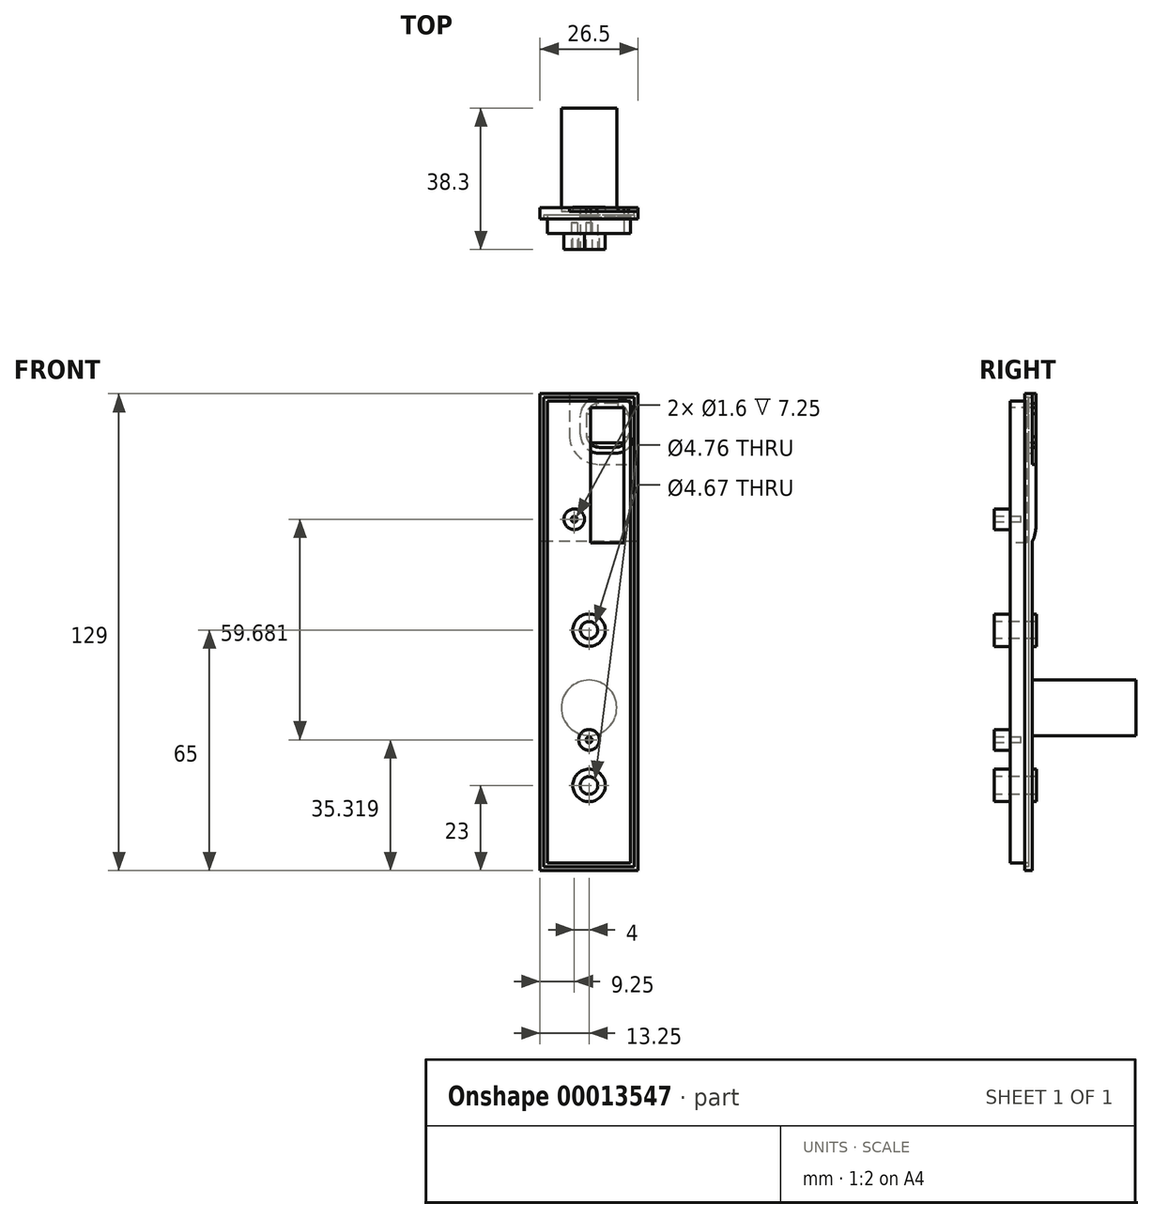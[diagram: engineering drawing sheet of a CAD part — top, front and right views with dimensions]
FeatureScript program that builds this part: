
annotation { "Feature Type Name" : "Feature", "Feature Type Description" : "" }
export const myFeature = defineFeature(function(context is Context, id is Id, definition is map)
    precondition{}
    {
        {
            var Q0;
            Q0=qCreatedBy(makeId("Front.planeOp"),FACE);
            var sketch = newSketch(context, id + "F0", { "sketchPlane" : qUnion([Q0])});
            skLineSegment(sketch, "E0.rect.bottom", {"start": v(13.25, -64.5) * mm, "end": v(-13.25, -64.5) * mm});
            skLineSegment(sketch, "E0.rect.top", {"start": v(13.25, 64.5) * mm, "end": v(-13.25, 64.5) * mm});
            skLineSegment(sketch, "E0.rect.left", {"start": v(13.25, -64.5) * mm, "end": v(13.25, 64.5) * mm});
            skLineSegment(sketch, "E0.rect.right", {"start": v(-13.25, -64.5) * mm, "end": v(-13.25, 64.5) * mm});
            skPoint(sketch, "E0.rect.middle", {"position": v(0, 0) * mm});
            skSolve(sketch);
        }
        {
            var Q0;
            Q0 = qSketchRegion(id + "F0", true);
            extrude(context, id + "F1", {"entities" : qUnion([Q0]), "depth" : 2 * mm});
        }
        {
            var Q0;
            Q0=makeQuery(id+"F1.opExtrude","CAP_FACE",FACE,{"disambiguationData":[OSD([sQuery(id+"F0.wireOp",EDGE,"E0.rect.bottom"),sQuery(id+"F0.wireOp",EDGE,"E0.rect.top"),sQuery(id+"F0.wireOp",EDGE,"E0.rect.left"),sQuery(id+"F0.wireOp",EDGE,"E0.rect.right")])],"isStart":false});
            var sketch = newSketch(context, id + "F2", { "sketchPlane" : qUnion([Q0])});
            skLineSegment(sketch, "E1.rect.bottom", {"start": v(12.25, 63.5) * mm, "end": v(-12.25, 63.5) * mm});
            skLineSegment(sketch, "E1.rect.top", {"start": v(12.25, -63.5) * mm, "end": v(-12.25, -63.5) * mm});
            skLineSegment(sketch, "E1.rect.left", {"start": v(12.25, 63.5) * mm, "end": v(12.25, -63.5) * mm});
            skLineSegment(sketch, "E1.rect.right", {"start": v(-12.25, 63.5) * mm, "end": v(-12.25, -63.5) * mm});
            skPoint(sketch, "E1.rect.middle", {"position": v(0, 0) * mm});
            skLineSegment(sketch, "E2.rect.bottom", {"start": v(11.25, 62.5) * mm, "end": v(-11.25, 62.5) * mm});
            skLineSegment(sketch, "E2.rect.top", {"start": v(11.25, -62.5) * mm, "end": v(-11.25, -62.5) * mm});
            skLineSegment(sketch, "E2.rect.left", {"start": v(11.25, 62.5) * mm, "end": v(11.25, -62.5) * mm});
            skLineSegment(sketch, "E2.rect.right", {"start": v(-11.25, 62.5) * mm, "end": v(-11.25, -62.5) * mm});
            skSolve(sketch);
        }
        {
            var Q0;
            Q0 = qSketchRegion(id + "F2", true);
            extrude(context, id + "F3", {"entities" : qUnion([Q0]), "operationType" : NewBodyOperationType.REMOVE, "oppositeDirection" : true, "depth" : 1 * mm});
        }
        {
            var Q0;
            Q0=makeQuery(id+"F1.opExtrude","CAP_FACE",FACE,{"disambiguationData":[OSD([sQuery(id+"F0.wireOp",EDGE,"E0.rect.bottom"),sQuery(id+"F0.wireOp",EDGE,"E0.rect.top"),sQuery(id+"F0.wireOp",EDGE,"E0.rect.left"),sQuery(id+"F0.wireOp",EDGE,"E0.rect.right")])],"isStart":true});
            var sketch = newSketch(context, id + "F4", { "sketchPlane" : qUnion([Q0])});
            skLineSegment(sketch, "E3.bottom", {"start": v(-13.25, 64.5) * mm, "end": v(13.25, 64.5) * mm});
            skLineSegment(sketch, "E3.top", {"start": v(-13.25, 24.5) * mm, "end": v(13.25, 24.5) * mm});
            skLineSegment(sketch, "E3.left", {"start": v(-13.25, 64.5) * mm, "end": v(-13.25, 24.5) * mm});
            skLineSegment(sketch, "E3.right", {"start": v(13.25, 64.5) * mm, "end": v(13.25, 24.5) * mm});
            skSolve(sketch);
        }
        {
            var Q0;
            Q0 = qSketchRegion(id + "F4", true);
            extrude(context, id + "F5", {"entities" : qUnion([Q0]), "operationType" : NewBodyOperationType.ADD, "depth" : 1 * mm});
        }
        {
            var Q0;
            Q0=makeQuery(id+"F5.opExtrude","CAP_EDGE",EDGE,{"disambiguationData":[OSD([sQuery(id+"F4.wireOp",EDGE,"E3.top")])],"isStart":false});
            fillet(context, id + "F6", {"entities" : qUnion([Q0]), "radius" : 10 * mm, "tangentPropagation" : true, "allowEdgeOverflow" : false});
        }
        {
            var Q0;
            Q0=makeQuery(id+"F3.boolean.opBoolean","SPLIT",FACE,{"disambiguationData":[TD([makeQuery(id+"F3.opExtrude","SWEPT_FACE",FACE,{"disambiguationData":[OSD([sQuery(id+"F2.wireOp",EDGE,"E2.rect.bottom")])]})])],"derivedFrom":makeQuery(id+"F1.opExtrude","CAP_FACE",FACE,{"disambiguationData":[OSD([sQuery(id+"F0.wireOp",EDGE,"E0.rect.bottom"),sQuery(id+"F0.wireOp",EDGE,"E0.rect.top"),sQuery(id+"F0.wireOp",EDGE,"E0.rect.left"),sQuery(id+"F0.wireOp",EDGE,"E0.rect.right")])],"isStart":false})});
            var sketch = newSketch(context, id + "F7", { "sketchPlane" : qUnion([Q0])});
            skLineSegment(sketch, "E4.bottom", {"start": v(9.45, 60.7) * mm, "end": v(0.45, 60.7) * mm});
            skLineSegment(sketch, "E4.top", {"start": v(0.45, 51.18) * mm, "end": v(9.45, 51.18) * mm});
            skLineSegment(sketch, "E4.left", {"start": v(9.45, 60.7) * mm, "end": v(9.45, 51.18) * mm});
            skLineSegment(sketch, "E4.right", {"start": v(0.45, 60.7) * mm, "end": v(0.45, 51.18) * mm});
            skSolve(sketch);
        }
        {
            var Q0;
            Q0=makeQuery(id+"F3.boolean.opBoolean","SPLIT",FACE,{"disambiguationData":[TD([makeQuery(id+"F3.opExtrude","SWEPT_FACE",FACE,{"disambiguationData":[OSD([sQuery(id+"F2.wireOp",EDGE,"E2.rect.bottom")])]})])],"derivedFrom":makeQuery(id+"F1.opExtrude","CAP_FACE",FACE,{"disambiguationData":[OSD([sQuery(id+"F0.wireOp",EDGE,"E0.rect.bottom"),sQuery(id+"F0.wireOp",EDGE,"E0.rect.top"),sQuery(id+"F0.wireOp",EDGE,"E0.rect.left"),sQuery(id+"F0.wireOp",EDGE,"E0.rect.right")])],"isStart":false})});
            var sketch = newSketch(context, id + "F8", { "sketchPlane" : qUnion([Q0])});
            skLineSegment(sketch, "E5.bottom", {"start": v(-11.25, 62.5) * mm, "end": v(11.25, 62.5) * mm});
            skLineSegment(sketch, "E5.top", {"start": v(-11.25, -62.5) * mm, "end": v(11.25, -62.5) * mm});
            skLineSegment(sketch, "E5.left", {"start": v(-11.25, 62.5) * mm, "end": v(-11.25, -62.5) * mm});
            skLineSegment(sketch, "E5.right", {"start": v(11.25, 62.5) * mm, "end": v(11.25, -62.5) * mm});
            skSolve(sketch);
        }
        {
            var Q0;
            Q0 = qSketchRegion(id + "F8", true);
            extrude(context, id + "F9", {"entities" : qUnion([Q0]), "operationType" : NewBodyOperationType.ADD, "depth" : 4 * mm});
        }
        {
            var Q0;
            Q0 = qSketchRegion(id + "F7", true);
            var Q1;
            Q1=makeQuery(id+"F5.opExtrude","CAP_FACE",FACE,{"disambiguationData":[OSD([sQuery(id+"F4.wireOp",EDGE,"E3.bottom"),sQuery(id+"F4.wireOp",EDGE,"E3.top"),sQuery(id+"F4.wireOp",EDGE,"E3.left"),sQuery(id+"F4.wireOp",EDGE,"E3.right")])],"isStart":false});
            extrude(context, id + "F10", {"entities" : qUnion([Q0]), "operationType" : NewBodyOperationType.REMOVE, "endBound" : BoundingType.UP_TO_SURFACE, "oppositeDirection" : true, "endBoundEntityFace" : qUnion([Q1]), "depth" : 25 * mm, "hasSecondDirection" : true, "secondDirectionOppositeDirection" : false, "secondDirectionDepth" : 10 * mm});
        }
        {
            var Q0;
            Q0=makeQuery(id+"F9.opExtrude","CAP_FACE",FACE,{"disambiguationData":[OSD([sQuery(id+"F8.wireOp",EDGE,"E5.bottom"),sQuery(id+"F8.wireOp",EDGE,"E5.top"),sQuery(id+"F8.wireOp",EDGE,"E5.left"),sQuery(id+"F8.wireOp",EDGE,"E5.right")])],"isStart":false});
            var sketch = newSketch(context, id + "F11", { "sketchPlane" : qUnion([Q0])});
            skLineSegment(sketch, "E6.bottom", {"start": v(0.45, 51.18) * mm, "end": v(9.45, 51.18) * mm});
            skLineSegment(sketch, "E6.top", {"start": v(0.45, 24.18) * mm, "end": v(9.45, 24.18) * mm});
            skLineSegment(sketch, "E6.left", {"start": v(0.45, 51.18) * mm, "end": v(0.45, 24.18) * mm});
            skLineSegment(sketch, "E6.right", {"start": v(9.45, 51.18) * mm, "end": v(9.45, 24.18) * mm});
            skSolve(sketch);
        }
        {
            var Q0;
            Q0 = qSketchRegion(id + "F11", true);
            var Q1;
            {var subQ0=sQuery(id+"F2.wireOp",EDGE,"E1.rect.bottom");var subQ1=sQuery(id+"F2.wireOp",EDGE,"E1.rect.top");var subQ2=sQuery(id+"F2.wireOp",EDGE,"E1.rect.left");var subQ3=sQuery(id+"F2.wireOp",EDGE,"E1.rect.right");var subQ4=sQuery(id+"F2.wireOp",EDGE,"E2.rect.bottom");var subQ5=sQuery(id+"F2.wireOp",EDGE,"E2.rect.top");var subQ6=sQuery(id+"F2.wireOp",EDGE,"E2.rect.left");var subQ7=sQuery(id+"F2.wireOp",EDGE,"E2.rect.right");Q1=makeQuery(id+"F26.boolean.opBoolean","SPLIT",FACE,{"disambiguationData":[TD([makeQuery(id+"F3.boolean.opBoolean","COPY",FACE,{"derivedFrom":makeQuery(id+"F3.opExtrude","SWEPT_FACE",FACE,{"disambiguationData":[OSD([subQ1])]})})])],"derivedFrom":makeQuery(id+"F3.boolean.opBoolean","COPY",FACE,{"derivedFrom":makeQuery(id+"F3.opExtrude","CAP_FACE",FACE,{"disambiguationData":[OSD([subQ0,subQ1,subQ2,subQ3,subQ4,subQ5,subQ6,subQ7])],"isStart":false})})});}
            extrude(context, id + "F12", {"entities" : qUnion([Q0]), "operationType" : NewBodyOperationType.REMOVE, "oppositeDirection" : true, "endBoundEntityFace" : qUnion([Q1]), "depth" : 4.5 * mm});
        }
        {
            var Q0;
            Q0=makeQuery(id+"F9.opExtrude","CAP_FACE",FACE,{"disambiguationData":[OSD([sQuery(id+"F8.wireOp",EDGE,"E5.bottom"),sQuery(id+"F8.wireOp",EDGE,"E5.top"),sQuery(id+"F8.wireOp",EDGE,"E5.left"),sQuery(id+"F8.wireOp",EDGE,"E5.right")])],"isStart":false});
            var sketch = newSketch(context, id + "F13", { "sketchPlane" : qUnion([Q0])});
            skLineSegment(sketch, "E7", {"start": v(-13.25, 64.5) * mm, "end": v(13.25, 64.5) * mm, "construction": true});
            skCircle(sketch, "E8", {"center": v(0, 0.5) * mm, "radius": 4.38 * mm});
            skLineSegment(sketch, "E9", {"start": v(-13.25, -84.5) * mm, "end": v(13.25, -84.5) * mm, "construction": true});
            skCircle(sketch, "E10", {"center": v(0, -41.5) * mm, "radius": 4.38 * mm});
            skPoint(sketch, "E11.rect.middle", {"position": v(0, -20.5) * mm});
            skCircle(sketch, "E12", {"center": v(0, -20.5) * mm, "radius": 7.5 * mm, "construction": true});
            skLineSegment(sketch, "E13", {"start": v(0, 64.5) * mm, "end": v(0, -84.5) * mm});
            skLineSegment(sketch, "E14", {"start": v(0, 0.5) * mm, "end": v(0, -20.5) * mm, "construction": true});
            skLineSegment(sketch, "E15", {"start": v(0, -20.5) * mm, "end": v(0, -41.5) * mm, "construction": true});
            skSolve(sketch);
        }
        {
            var Q0;
            Q0 = qSketchRegion(id + "F13", true);
            var Q1;
            Q1=makeQuery(id+"F22.opExtrude","CAP_FACE",FACE,{"disambiguationData":[OSD([sQuery(id+"F21.wireOp",EDGE,"E30")])],"isStart":false});
            extrude(context, id + "F14", {"entities" : qUnion([Q0]), "operationType" : NewBodyOperationType.ADD, "endBoundEntityFace" : qUnion([Q1]), "depth" : 4.3 * mm});
        }
        {
            var Q0;
            {var subQ0=sQuery(id+"F0.wireOp",EDGE,"E0.rect.bottom");var subQ1=sQuery(id+"F0.wireOp",EDGE,"E0.rect.top");var subQ2=sQuery(id+"F0.wireOp",EDGE,"E0.rect.left");var subQ3=sQuery(id+"F0.wireOp",EDGE,"E0.rect.right");Q0=makeQuery(id+"FUutNJTZsO6T2Ni_1.boolean.opBoolean","SPLIT",FACE,{"disambiguationData":[TD([makeQuery(id+"F1.opExtrude","SWEPT_FACE",FACE,{"disambiguationData":[OSD([subQ0])]})])],"derivedFrom":makeQuery(id+"F1.opExtrude","CAP_FACE",FACE,{"disambiguationData":[OSD([subQ0,subQ1,subQ2,subQ3])],"isStart":true})});}
            var sketch = newSketch(context, id + "F15", { "sketchPlane" : qUnion([Q0])});
            skLineSegment(sketch, "E16.rect.bottom", {"start": v(13.25, -64.5) * mm, "end": v(-13.25, -64.5) * mm, "construction": true});
            skPoint(sketch, "E16.rect.middle", {"position": v(0, -20.5) * mm});
            skCircle(sketch, "E17", {"center": v(0, -20.5) * mm, "radius": 7.5 * mm});
            skLineSegment(sketch, "E18.rect.top", {"start": v(13.25, 15) * mm, "end": v(-13.25, 15) * mm, "construction": true});
            skLineSegment(sketch, "E18.rect.left", {"start": v(13.25, -64.5) * mm, "end": v(13.25, 15) * mm, "construction": true});
            skLineSegment(sketch, "E18.rect.right", {"start": v(-13.25, -64.5) * mm, "end": v(-13.25, 15) * mm, "construction": true});
            skLineSegment(sketch, "E19", {"start": v(-13.25, -44.5) * mm, "end": v(13.25, -44.5) * mm, "construction": true});
            skLineSegment(sketch, "E20", {"start": v(0, 15) * mm, "end": v(0, -44.5) * mm});
            skSolve(sketch);
        }
        {
            var Q0;
            Q0 = qSketchRegion(id + "F15", true);
            extrude(context, id + "F16", {"entities" : qUnion([Q0]), "operationType" : NewBodyOperationType.ADD, "depth" : 28 * mm});
        }
        {
            var Q0;
            Q0=makeQuery(id+"F14.opExtrude","CAP_FACE",FACE,{"disambiguationData":[OSD([sQuery(id+"F13.wireOp",EDGE,"E8")])],"isStart":false});
            var sketch = newSketch(context, id + "F17", { "sketchPlane" : qUnion([Q0])});
            skCircle(sketch, "E21", {"center": v(0, 0.5) * mm, "radius": 2.34 * mm});
            skCircle(sketch, "E22", {"center": v(0, -41.5) * mm, "radius": 2.38 * mm});
            skLineSegment(sketch, "E23", {"start": v(-4.38, -23.42) * mm, "end": v(-4.38, -59.58) * mm, "construction": true});
            skLineSegment(sketch, "E24", {"start": v(-4.38, -41.5) * mm, "end": v(4.38, -41.5) * mm, "construction": true});
            skLineSegment(sketch, "E25", {"start": v(4.38, -23.94) * mm, "end": v(4.38, -59.06) * mm, "construction": true});
            skSolve(sketch);
        }
        {
            var Q0;
            Q0 = qSketchRegion(id + "F17", true);
            var Q1;
            {var subQ0=sQuery(id+"F0.wireOp",EDGE,"E0.rect.bottom");var subQ1=sQuery(id+"F0.wireOp",EDGE,"E0.rect.top");var subQ2=sQuery(id+"F0.wireOp",EDGE,"E0.rect.left");var subQ3=sQuery(id+"F0.wireOp",EDGE,"E0.rect.right");Q1=makeQuery(id+"FUutNJTZsO6T2Ni_1.boolean.opBoolean","SPLIT",FACE,{"disambiguationData":[TD([makeQuery(id+"F1.opExtrude","SWEPT_FACE",FACE,{"disambiguationData":[OSD([subQ0])]})])],"derivedFrom":makeQuery(id+"F1.opExtrude","CAP_FACE",FACE,{"disambiguationData":[OSD([subQ0,subQ1,subQ2,subQ3])],"isStart":true})});}
            extrude(context, id + "F18", {"entities" : qUnion([Q0]), "operationType" : NewBodyOperationType.REMOVE, "endBound" : BoundingType.UP_TO_SURFACE, "oppositeDirection" : true, "endBoundEntityFace" : qUnion([Q1]), "depth" : 25 * mm});
        }
        {
            var Q0;
            Q0=makeQuery(id+"F1.opExtrude","CAP_FACE",FACE,{"disambiguationData":[OSD([sQuery(id+"F0.wireOp",EDGE,"E0.rect.bottom"),sQuery(id+"F0.wireOp",EDGE,"E0.rect.top"),sQuery(id+"F0.wireOp",EDGE,"E0.rect.left"),sQuery(id+"F0.wireOp",EDGE,"E0.rect.right")])],"isStart":true});
            var sketch = newSketch(context, id + "F19", { "sketchPlane" : qUnion([Q0])});
            skCircle(sketch, "E26", {"center": v(0, 0.5) * mm, "radius": 4.38 * mm});
            skCircle(sketch, "E27", {"center": v(0, -41.5) * mm, "radius": 4.38 * mm});
            skCircle(sketch, "E28", {"center": v(0, 0.5) * mm, "radius": 2.34 * mm});
            skCircle(sketch, "E29", {"center": v(0, -41.5) * mm, "radius": 2.38 * mm});
            skSolve(sketch);
        }
        {
            var Q0;
            Q0 = qSketchRegion(id + "F19", true);
            var Q1;
            Q1=makeQuery(id+"FYc0KWkVzcQ2oCy_1.opExtrude","CAP_FACE",FACE,{"disambiguationData":[OSD([sQuery(id+"FxuQVQ8lCj4RhZQ_1.wireOp",EDGE,"0cf9ba85-6238-448b-8cd4-287eee810c51"),sQuery(id+"FxuQVQ8lCj4RhZQ_1.wireOp",EDGE,"b4d6cc2d-1f40-4273-a731-eaf728491af3"),sQuery(id+"FxuQVQ8lCj4RhZQ_1.wireOp",EDGE,"2b8fa5e3-a44b-4fcd-ac30-cf5bcc63a190"),sQuery(id+"FxuQVQ8lCj4RhZQ_1.wireOp",EDGE,"7435658f-580f-4094-b339-7dbd427cc99e"),sQuery(id+"FxuQVQ8lCj4RhZQ_1.wireOp",EDGE,"d7350775-b11e-431e-9dc7-10f8101245b6"),sQuery(id+"FxuQVQ8lCj4RhZQ_1.wireOp",EDGE,"a26f8e06-f1dd-4987-aab8-03ba0d05554c")])],"isStart":false});
            extrude(context, id + "F20", {"entities" : qUnion([Q0]), "operationType" : NewBodyOperationType.ADD, "endBoundEntityFace" : qUnion([Q1]), "depth" : 1.1 * mm});
        }
        {
            var Q0;
            Q0=makeQuery(id+"F9.opExtrude","CAP_FACE",FACE,{"disambiguationData":[OSD([sQuery(id+"F8.wireOp",EDGE,"E5.bottom"),sQuery(id+"F8.wireOp",EDGE,"E5.top"),sQuery(id+"F8.wireOp",EDGE,"E5.left"),sQuery(id+"F8.wireOp",EDGE,"E5.right")])],"isStart":false});
            var sketch = newSketch(context, id + "F21", { "sketchPlane" : qUnion([Q0])});
            skCircle(sketch, "E30", {"center": v(-4, 30.5) * mm, "radius": 2.8 * mm});
            skLineSegment(sketch, "E31.rect.bottom", {"start": v(13.25, -95.5) * mm, "end": v(-13.25, -95.5) * mm, "construction": true});
            skLineSegment(sketch, "E31.rect.top", {"start": v(13.25, 64.5) * mm, "end": v(-13.25, 64.5) * mm, "construction": true});
            skLineSegment(sketch, "E31.rect.right", {"start": v(-13.25, -95.5) * mm, "end": v(-13.25, 64.5) * mm, "construction": true});
            skPoint(sketch, "E31.rect.middle", {"position": v(0, -15.5) * mm});
            skLineSegment(sketch, "E32", {"start": v(13.25, -95.5) * mm, "end": v(13.25, 64.5) * mm, "construction": true});
            skCircle(sketch, "E33.1.MirrorC", {"center": v(0, -29.18) * mm, "radius": 2.8 * mm});
            skLineSegment(sketch, "E34", {"start": v(0, -95.5) * mm, "end": v(0, 64.5) * mm, "construction": true});
            skPoint(sketch, "E35", {"position": v(0, -41.5) * mm});
            skSolve(sketch);
        }
        {
            var Q0;
            Q0 = qSketchRegion(id + "F21", true);
            var Q2;
            Q2=makeQuery(id+"F14.opExtrude","CAP_FACE",FACE,{"disambiguationData":[OSD([sQuery(id+"F13.wireOp",EDGE,"E8")])],"isStart":false});
            extrude(context, id + "F22", {"entities" : qUnion([Q0]), "operationType" : NewBodyOperationType.ADD, "endBound" : BoundingType.UP_TO_SURFACE, "depth" : 8.8 * mm, "endBoundEntityFace" : qUnion([Q2])});
        }
        {
            var Q0;
            Q0=makeQuery(id+"F22.opExtrude","CAP_FACE",FACE,{"disambiguationData":[OSD([sQuery(id+"F21.wireOp",EDGE,"E30")])],"isStart":false});
            var sketch = newSketch(context, id + "F23", { "sketchPlane" : qUnion([Q0])});
            skCircle(sketch, "E36", {"center": v(-4, 30.5) * mm, "radius": 0.8 * mm});
            skLineSegment(sketch, "E37", {"start": v(0, 31.38) * mm, "end": v(0, -26.38) * mm, "construction": true});
            skLineSegment(sketch, "E38", {"start": v(0, 2.5) * mm, "end": v(-11.25, 2.5) * mm, "construction": true});
            skCircle(sketch, "E39.0.MirrorC", {"center": v(0, -29.18) * mm, "radius": 0.8 * mm});
            skSolve(sketch);
        }
        {
            var Q0;
            Q0 = qSketchRegion(id + "F23", true);
            extrude(context, id + "F24", {"entities" : qUnion([Q0]), "operationType" : NewBodyOperationType.REMOVE, "oppositeDirection" : true, "depth" : 7.25 * mm});
        }
        {
            var Q0;
            Q0=makeQuery(id+"F5.opExtrude","CAP_FACE",FACE,{"disambiguationData":[OSD([sQuery(id+"F4.wireOp",EDGE,"E3.bottom"),sQuery(id+"F4.wireOp",EDGE,"E3.top"),sQuery(id+"F4.wireOp",EDGE,"E3.left"),sQuery(id+"F4.wireOp",EDGE,"E3.right")])],"isStart":false});
            var sketch = newSketch(context, id + "F25", { "sketchPlane" : qUnion([Q0])});
            skLineSegment(sketch, "E40.bottom", {"start": v(-7.15, 61.9) * mm, "end": v(-2.75, 61.9) * mm});
            skLineSegment(sketch, "E40.top", {"start": v(-7.15, 49.98) * mm, "end": v(-2.75, 49.98) * mm});
            skLineSegment(sketch, "E40.left", {"start": v(-10.65, 58.4) * mm, "end": v(-10.65, 53.48) * mm});
            skLineSegment(sketch, "E40.right", {"start": v(0.75, 58.4) * mm, "end": v(0.75, 53.48) * mm});
            skPoint(sketch, "E41.visualSharp", {"position": v(-10.65, 61.9) * mm});
            skArc(sketch, "E41.filletArc", {"start": v(-7.15, 61.9) * mm, "mid": v(-9.62, 60.87) * mm, "end": v(-10.65, 58.4) * mm});
            skPoint(sketch, "E42.visualSharp", {"position": v(0.75, 61.9) * mm});
            skArc(sketch, "E42.filletArc", {"start": v(0.75, 58.4) * mm, "mid": v(-0.28, 60.87) * mm, "end": v(-2.75, 61.9) * mm});
            skPoint(sketch, "E43.visualSharp", {"position": v(0.75, 49.98) * mm});
            skArc(sketch, "E43.filletArc", {"start": v(-2.75, 49.98) * mm, "mid": v(-0.28, 51) * mm, "end": v(0.75, 53.48) * mm});
            skPoint(sketch, "E44.visualSharp", {"position": v(-10.65, 49.98) * mm});
            skArc(sketch, "E44.filletArc", {"start": v(-10.65, 53.48) * mm, "mid": v(-9.62, 51) * mm, "end": v(-7.15, 49.98) * mm});
            skLineSegment(sketch, "E45.0", {"start": v(-7.15, 63.5) * mm, "end": v(-2.75, 63.5) * mm});
            skArc(sketch, "E45.1", {"start": v(2.35, 58.4) * mm, "mid": v(0.86, 62) * mm, "end": v(-2.75, 63.5) * mm});
            skArc(sketch, "E45.2", {"start": v(-7.15, 63.5) * mm, "mid": v(-10.76, 62) * mm, "end": v(-12.25, 58.4) * mm});
            skLineSegment(sketch, "E45.3", {"start": v(2.35, 58.4) * mm, "end": v(2.35, 53.48) * mm});
            skLineSegment(sketch, "E45.4", {"start": v(-12.25, 58.4) * mm, "end": v(-12.25, 53.48) * mm});
            skArc(sketch, "E45.5", {"start": v(-12.25, 53.48) * mm, "mid": v(-10.76, 49.87) * mm, "end": v(-7.15, 48.38) * mm});
            skLineSegment(sketch, "E45.6", {"start": v(-7.15, 48.38) * mm, "end": v(-2.75, 48.38) * mm});
            skArc(sketch, "E45.7", {"start": v(-2.75, 48.38) * mm, "mid": v(0.86, 49.87) * mm, "end": v(2.35, 53.48) * mm});
            skSolve(sketch);
        }
        {
            var Q0;
            Q0 = qSketchRegion(id + "F25", true);
            var Q1;
            Q1=makeQuery(id+"F12.boolean.opBoolean","COPY",FACE,{"derivedFrom":makeQuery(id+"F12.opExtrude","CAP_FACE",FACE,{"disambiguationData":[OSD([sQuery(id+"F11.wireOp",EDGE,"E6.bottom"),sQuery(id+"F11.wireOp",EDGE,"E6.top"),sQuery(id+"F11.wireOp",EDGE,"E6.left"),sQuery(id+"F11.wireOp",EDGE,"E6.right")])],"isStart":false})});
            extrude(context, id + "F26", {"entities" : qUnion([Q0]), "operationType" : NewBodyOperationType.REMOVE, "endBound" : BoundingType.UP_TO_SURFACE, "oppositeDirection" : true, "endBoundEntityFace" : qUnion([Q1]), "depth" : 3 * mm});
        }
        {
            var Q0;
            {var subQ0=sQuery(id+"F4.wireOp",EDGE,"E3.bottom");var subQ1=sQuery(id+"F4.wireOp",EDGE,"E3.top");var subQ2=sQuery(id+"F4.wireOp",EDGE,"E3.left");var subQ3=sQuery(id+"F4.wireOp",EDGE,"E3.right");Q0=makeQuery(id+"F26.boolean.opBoolean","SPLIT",FACE,{"disambiguationData":[TD([makeQuery(id+"F1.opExtrude","SWEPT_FACE",FACE,{"disambiguationData":[OSD([sQuery(id+"F0.wireOp",EDGE,"E0.rect.top")])]})])],"derivedFrom":makeQuery(id+"F5.opExtrude","CAP_FACE",FACE,{"disambiguationData":[OSD([subQ0,subQ1,subQ2,subQ3])],"isStart":false})});}
            var sketch = newSketch(context, id + "F27", { "sketchPlane" : qUnion([Q0])});
            skLineSegment(sketch, "E46", {"start": v(5.35, 64.5) * mm, "end": v(5.35, 53.38) * mm});
            skLineSegment(sketch, "E47", {"start": v(-2.65, 45.38) * mm, "end": v(-13.25, 45.38) * mm});
            skPoint(sketch, "E48.visualSharp", {"position": v(5.35, 45.38) * mm});
            skArc(sketch, "E48.filletArc", {"start": v(-2.65, 45.38) * mm, "mid": v(3, 47.72) * mm, "end": v(5.35, 53.38) * mm});
            skLineSegment(sketch, "E49.bottom", {"start": v(-7.65, 61.9) * mm, "end": v(-2.25, 61.9) * mm});
            skLineSegment(sketch, "E49.top", {"start": v(-7.65, 49.98) * mm, "end": v(-2.25, 49.98) * mm});
            skLineSegment(sketch, "E49.left", {"start": v(-10.65, 58.9) * mm, "end": v(-10.65, 52.98) * mm});
            skLineSegment(sketch, "E49.right", {"start": v(0.75, 58.9) * mm, "end": v(0.75, 52.98) * mm});
            skPoint(sketch, "E50.visualSharp", {"position": v(-10.65, 61.9) * mm});
            skArc(sketch, "E50.filletArc", {"start": v(-7.65, 61.9) * mm, "mid": v(-9.77, 61.02) * mm, "end": v(-10.65, 58.9) * mm});
            skPoint(sketch, "E51.visualSharp", {"position": v(0.75, 61.9) * mm});
            skArc(sketch, "E51.filletArc", {"start": v(0.75, 58.9) * mm, "mid": v(-0.13, 61.02) * mm, "end": v(-2.25, 61.9) * mm});
            skPoint(sketch, "E52.visualSharp", {"position": v(0.75, 49.98) * mm});
            skArc(sketch, "E52.filletArc", {"start": v(-2.25, 49.98) * mm, "mid": v(-0.13, 50.85) * mm, "end": v(0.75, 52.98) * mm});
            skPoint(sketch, "E53.visualSharp", {"position": v(-10.65, 49.98) * mm});
            skArc(sketch, "E53.filletArc", {"start": v(-10.65, 52.98) * mm, "mid": v(-9.77, 50.85) * mm, "end": v(-7.65, 49.98) * mm});
            skLineSegment(sketch, "E54", {"start": v(5.35, 64.5) * mm, "end": v(-13.25, 64.5) * mm});
            skLineSegment(sketch, "E55", {"start": v(-13.25, 64.5) * mm, "end": v(-13.25, 45.38) * mm});
            skSolve(sketch);
        }
        {
            var Q0;
            Q0 = qSketchRegion(id + "F27", true);
            extrude(context, id + "F28", {"entities" : qUnion([Q0]), "operationType" : NewBodyOperationType.REMOVE, "oppositeDirection" : true, "depth" : 1 * mm});
        }
        {
            var Q0;
            Q0=makeQuery(id+"F26.boolean.opBoolean","SPLIT",FACE,{"disambiguationData":[TD([makeQuery(id+"F10.boolean.opBoolean","COPY",FACE,{"derivedFrom":makeQuery(id+"F10.opExtrude","SWEPT_FACE",FACE,{"disambiguationData":[OSD([sQuery(id+"F7.wireOp",EDGE,"E4.bottom")])]})})])],"derivedFrom":makeQuery(id+"F5.opExtrude","CAP_FACE",FACE,{"disambiguationData":[OSD([sQuery(id+"F4.wireOp",EDGE,"E3.bottom"),sQuery(id+"F4.wireOp",EDGE,"E3.top"),sQuery(id+"F4.wireOp",EDGE,"E3.left"),sQuery(id+"F4.wireOp",EDGE,"E3.right")])],"isStart":false})});
            var sketch = newSketch(context, id + "F29", { "sketchPlane" : qUnion([Q0])});
            skLineSegment(sketch, "E56.rect.bottom", {"start": v(-7.85, 59.1) * mm, "end": v(-11.05, 59.1) * mm});
            skLineSegment(sketch, "E56.rect.top", {"start": v(-7.85, 62.3) * mm, "end": v(-11.05, 62.3) * mm});
            skLineSegment(sketch, "E56.rect.left", {"start": v(-7.85, 59.1) * mm, "end": v(-7.85, 62.3) * mm});
            skLineSegment(sketch, "E56.rect.right", {"start": v(-11.05, 59.1) * mm, "end": v(-11.05, 62.3) * mm});
            skPoint(sketch, "E56.rect.middle", {"position": v(-9.45, 60.7) * mm});
            skLineSegment(sketch, "E57.rect.bottom", {"start": v(1.15, 59.1) * mm, "end": v(-2.05, 59.1) * mm});
            skLineSegment(sketch, "E57.rect.top", {"start": v(1.15, 62.3) * mm, "end": v(-2.05, 62.3) * mm});
            skLineSegment(sketch, "E57.rect.left", {"start": v(1.15, 59.1) * mm, "end": v(1.15, 62.3) * mm});
            skLineSegment(sketch, "E57.rect.right", {"start": v(-2.05, 59.1) * mm, "end": v(-2.05, 62.3) * mm});
            skPoint(sketch, "E57.rect.middle", {"position": v(-0.45, 60.7) * mm});
            skLineSegment(sketch, "E58.rect.bottom", {"start": v(1.15, 49.58) * mm, "end": v(-2.05, 49.58) * mm});
            skLineSegment(sketch, "E58.rect.top", {"start": v(1.15, 52.78) * mm, "end": v(-2.05, 52.78) * mm});
            skLineSegment(sketch, "E58.rect.left", {"start": v(1.15, 49.58) * mm, "end": v(1.15, 52.78) * mm});
            skLineSegment(sketch, "E58.rect.right", {"start": v(-2.05, 49.58) * mm, "end": v(-2.05, 52.78) * mm});
            skPoint(sketch, "E58.rect.middle", {"position": v(-0.45, 51.18) * mm});
            skLineSegment(sketch, "E59.rect.bottom", {"start": v(-7.85, 49.58) * mm, "end": v(-11.05, 49.58) * mm});
            skLineSegment(sketch, "E59.rect.top", {"start": v(-7.85, 52.78) * mm, "end": v(-11.05, 52.78) * mm});
            skLineSegment(sketch, "E59.rect.left", {"start": v(-7.85, 49.58) * mm, "end": v(-7.85, 52.78) * mm});
            skLineSegment(sketch, "E59.rect.right", {"start": v(-11.05, 49.58) * mm, "end": v(-11.05, 52.78) * mm});
            skPoint(sketch, "E59.rect.middle", {"position": v(-9.45, 51.18) * mm});
            skSolve(sketch);
        }
        {
            var Q0;
            Q0 = qSketchRegion(id + "F29", true);
            var Q1;
            Q1=makeQuery(id+"F28.boolean.opBoolean","COPY",FACE,{"derivedFrom":makeQuery(id+"F28.opExtrude","CAP_FACE",FACE,{"disambiguationData":[OSD([sQuery(id+"F27.wireOp",EDGE,"E46"),sQuery(id+"F27.wireOp",EDGE,"E47"),sQuery(id+"F27.wireOp",EDGE,"E48.filletArc"),sQuery(id+"F27.wireOp",EDGE,"E49.bottom"),sQuery(id+"F27.wireOp",EDGE,"E49.top"),sQuery(id+"F27.wireOp",EDGE,"E49.left"),sQuery(id+"F27.wireOp",EDGE,"E49.right"),sQuery(id+"F27.wireOp",EDGE,"E50.filletArc"),sQuery(id+"F27.wireOp",EDGE,"E51.filletArc"),sQuery(id+"F27.wireOp",EDGE,"E52.filletArc"),sQuery(id+"F27.wireOp",EDGE,"E53.filletArc"),sQuery(id+"F27.wireOp",EDGE,"E54"),sQuery(id+"F27.wireOp",EDGE,"E55")])],"isStart":false})});
            extrude(context, id + "F30", {"entities" : qUnion([Q0]), "operationType" : NewBodyOperationType.REMOVE, "endBound" : BoundingType.UP_TO_SURFACE, "oppositeDirection" : true, "endBoundEntityFace" : qUnion([Q1]), "depth" : 25 * mm});
        }
    });
